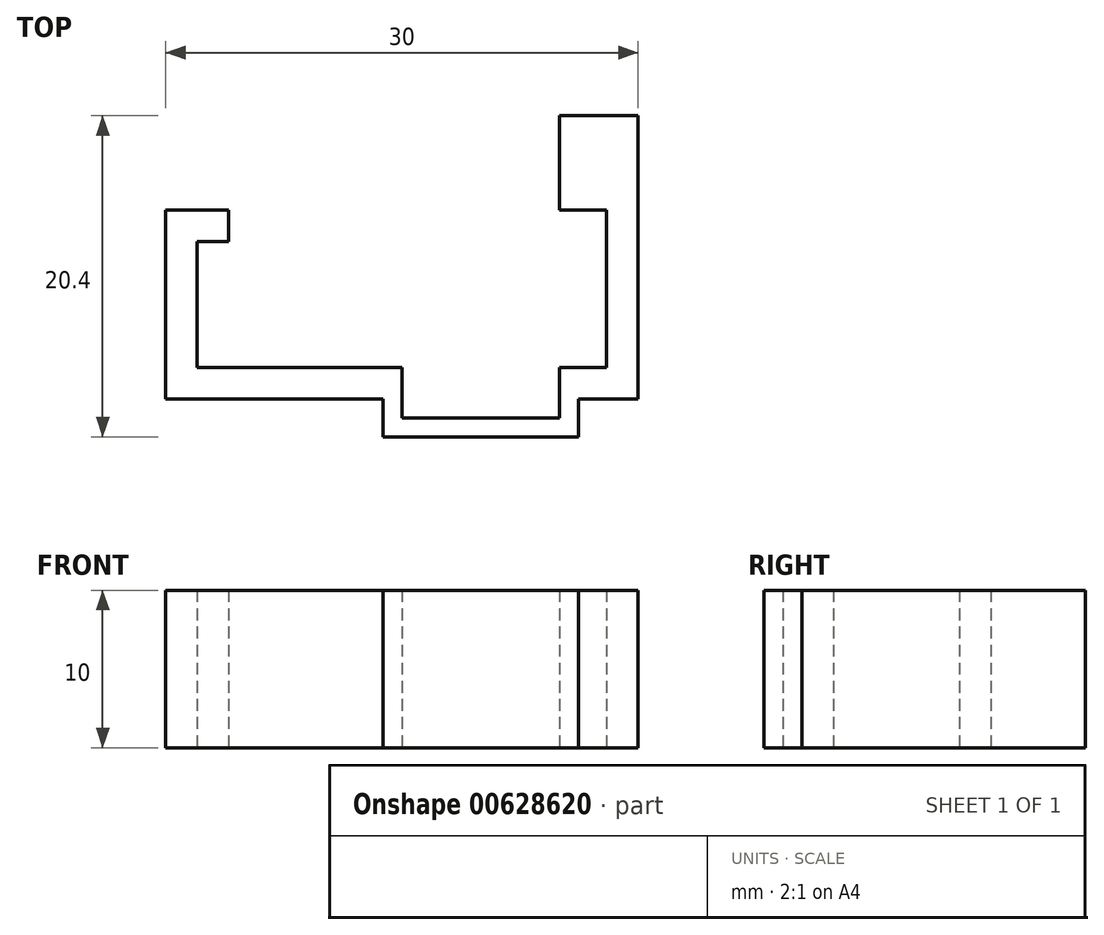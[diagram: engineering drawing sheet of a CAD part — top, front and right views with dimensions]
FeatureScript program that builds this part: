
annotation { "Feature Type Name" : "Feature", "Feature Type Description" : "" }
export const myFeature = defineFeature(function(context is Context, id is Id, definition is map)
    precondition{}
    {
        {
            var Q0;
            Q0=qCreatedBy(makeId("Top.planeOp"),FACE);
            var sketch = newSketch(context, id + "F0", { "sketchPlane" : qUnion([Q0])});
            skLineSegment(sketch, "E0.bottom", {"start": v(0, 0) * mm, "end": v(-26, 0) * mm});
            skLineSegment(sketch, "E0.top", {"start": v(0, 2) * mm, "end": v(-26, 2) * mm});
            skLineSegment(sketch, "E0.left", {"start": v(0, 0) * mm, "end": v(0, 2) * mm});
            skLineSegment(sketch, "E0.right", {"start": v(-26, 0) * mm, "end": v(-26, 2) * mm});
            skLineSegment(sketch, "E1.bottom", {"start": v(-13, 0) * mm, "end": v(-3, 0) * mm, "construction": true});
            skLineSegment(sketch, "E1.top", {"start": v(-13, -1.2) * mm, "end": v(-3, -1.2) * mm});
            skLineSegment(sketch, "E1.left", {"start": v(-13, 0) * mm, "end": v(-13, -1.2) * mm});
            skLineSegment(sketch, "E1.right", {"start": v(-3, 0) * mm, "end": v(-3, -1.2) * mm});
            skLineSegment(sketch, "E2.bottom", {"start": v(0, 0) * mm, "end": v(2, 0) * mm});
            skLineSegment(sketch, "E2.top", {"start": v(0, 18) * mm, "end": v(2, 18) * mm});
            skLineSegment(sketch, "E2.left", {"start": v(0, 0) * mm, "end": v(0, 18) * mm});
            skLineSegment(sketch, "E2.right", {"start": v(2, 0) * mm, "end": v(2, 18) * mm});
            skLineSegment(sketch, "E3.bottom", {"start": v(-26, 0) * mm, "end": v(-28, 0) * mm});
            skLineSegment(sketch, "E3.top", {"start": v(-26, 10) * mm, "end": v(-28, 10) * mm});
            skLineSegment(sketch, "E3.left", {"start": v(-26, 0) * mm, "end": v(-26, 10) * mm});
            skLineSegment(sketch, "E3.right", {"start": v(-28, 0) * mm, "end": v(-28, 10) * mm});
            skLineSegment(sketch, "E4.bottom", {"start": v(-28, 10) * mm, "end": v(-24, 10) * mm});
            skLineSegment(sketch, "E4.top", {"start": v(-28, 12) * mm, "end": v(-24, 12) * mm});
            skLineSegment(sketch, "E4.left", {"start": v(-28, 10) * mm, "end": v(-28, 12) * mm});
            skLineSegment(sketch, "E4.right", {"start": v(-24, 10) * mm, "end": v(-24, 12) * mm});
            skLineSegment(sketch, "E5", {"start": v(-13, 0) * mm, "end": v(-13, 2) * mm});
            skLineSegment(sketch, "E6", {"start": v(-3, 0) * mm, "end": v(-3, 2) * mm});
            skLineSegment(sketch, "E7.0", {"start": v(-1.8, 0) * mm, "end": v(-1.8, -2.4) * mm});
            skLineSegment(sketch, "E7.1", {"start": v(-14.2, -2.4) * mm, "end": v(-1.8, -2.4) * mm});
            skLineSegment(sketch, "E7.2", {"start": v(-14.2, 0) * mm, "end": v(-14.2, -2.4) * mm});
            skLineSegment(sketch, "E8.bottom", {"start": v(0, 18) * mm, "end": v(-3, 18) * mm});
            skLineSegment(sketch, "E8.top", {"start": v(0, 12) * mm, "end": v(-3, 12) * mm});
            skLineSegment(sketch, "E8.left", {"start": v(0, 18) * mm, "end": v(0, 12) * mm});
            skLineSegment(sketch, "E8.right", {"start": v(-3, 18) * mm, "end": v(-3, 12) * mm});
            skSolve(sketch);
        }
        {
            var Q0;
            Q0=makeQuery(id+"F0.imprint","IMPRINT",FACE,{"disambiguationData":[TD([[makeQuery(id+"F0.imprint","IMPRINT",EDGE,{"derivedFrom":sQuery(id+"F0.wireOp",EDGE,"E4.top")}),-1.0]])]});
            var Q1;
            {var subQ5=sQuery(id+"F0.wireOp",EDGE,"E3.bottom");Q1=makeQuery(id+"F0.imprint","IMPRINT",FACE,{"disambiguationData":[TD([[makeQuery(id+"F0.imprint","IMPRINT",EDGE,{"derivedFrom":subQ5}),-1.0]])]});}
            var Q2;
            {var subQ3=sQuery(id+"F0.wireOp",EDGE,"E5");Q2=makeQuery(id+"F0.imprint","IMPRINT",FACE,{"disambiguationData":[TD([[makeQuery(id+"F0.imprint","IMPRINT",EDGE,{"derivedFrom":subQ3}),1.0]])]});}
            var Q3;
            Q3=makeQuery(id+"F0.imprint","IMPRINT",FACE,{"disambiguationData":[TD([[makeQuery(id+"F0.imprint","IMPRINT",EDGE,{"derivedFrom":sQuery(id+"F0.wireOp",EDGE,"E1.top")}),-1.0]])]});
            var Q4;
            {var subQ5=sQuery(id+"F0.wireOp",EDGE,"E6");Q4=makeQuery(id+"F0.imprint","IMPRINT",FACE,{"disambiguationData":[TD([[makeQuery(id+"F0.imprint","IMPRINT",EDGE,{"derivedFrom":subQ5}),-1.0]])]});}
            var Q5;
            {var subQ3=sQuery(id+"F0.wireOp",EDGE,"E2.bottom");Q5=makeQuery(id+"F0.imprint","IMPRINT",FACE,{"disambiguationData":[TD([[makeQuery(id+"F0.imprint","IMPRINT",EDGE,{"derivedFrom":subQ3}),1.0]])]});}
            var Q6;
            Q6=makeQuery(id+"F0.imprint","IMPRINT",FACE,{"disambiguationData":[TD([[makeQuery(id+"F0.imprint","IMPRINT",EDGE,{"derivedFrom":sQuery(id+"F0.wireOp",EDGE,"E8.bottom")}),1.0]])]});
            extrude(context, id + "F1", {"entities" : qUnion([Q0, Q1, Q2, Q3, Q4, Q5, Q6]), "endBound" : BoundingType.SYMMETRIC, "depth" : 10 * mm, "offsetDistance" : 25 * mm});
        }
    });
